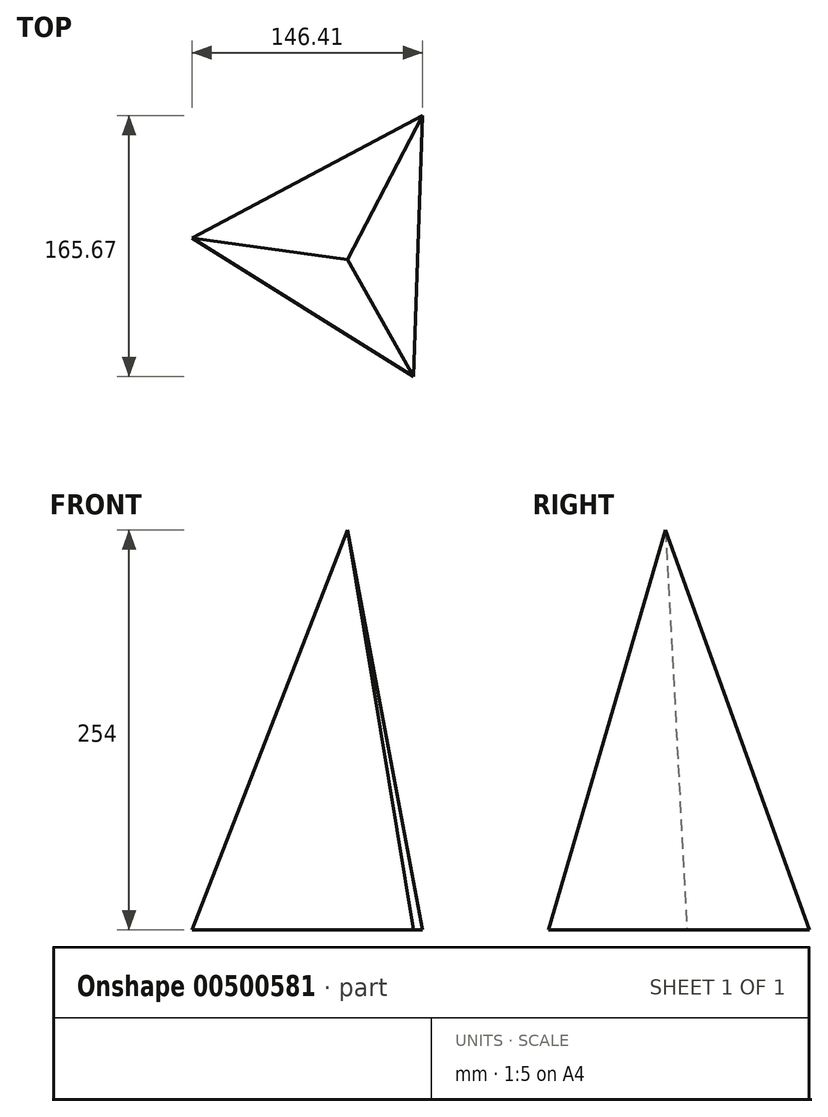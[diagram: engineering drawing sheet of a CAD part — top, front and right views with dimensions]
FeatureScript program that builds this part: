
annotation { "Feature Type Name" : "Feature", "Feature Type Description" : "" }
export const myFeature = defineFeature(function(context is Context, id is Id, definition is map)
    precondition{}
    {
        {
            var Q0;
            Q0=qCreatedBy(makeId("Top.planeOp"),FACE);
            var sketch = newSketch(context, id + "F0", { "sketchPlane" : qUnion([Q0])});
            skCircle(sketch, "E0.cCircle", {"center": v(0, 12.68) * mm, "radius": 95.7 * mm, "construction": true});
            skLineSegment(sketch, "E0.0", {"start": v(44.89, -71.85) * mm, "end": v(-95.65, 16.07) * mm});
            skLineSegment(sketch, "E0.1", {"start": v(-95.65, 16.07) * mm, "end": v(50.76, 93.82) * mm});
            skLineSegment(sketch, "E0.2", {"start": v(50.76, 93.82) * mm, "end": v(44.89, -71.85) * mm});
            skSolve(sketch);
        }
        {
            var Q0;
            Q0=qCreatedBy(makeId("Top.planeOp"),FACE);
            cPlane(context, id + "F1", {"entities" : qUnion([Q0]), "cplaneType" : CPlaneType.OFFSET, "offset" : 254 * mm, "width" : 152.4 * mm, "height" : 152.4 * mm});
        }
        {
            var Q0;
            Q0=qCreatedBy(id+"F1.planeOp",FACE);
            var sketch = newSketch(context, id + "F2", { "sketchPlane" : qUnion([Q0])});
            skPoint(sketch, "E1", {"position": v(3.2, 2.48) * mm});
            skSolve(sketch);
        }
        {
            var Q0;
            Q0=sQuery(id+"F2.wireOp",VERTEX,"E1");
            var Q1;
            Q1=makeQuery(id+"F0.imprint","IMPRINT",FACE,{"disambiguationData":[TD([[makeQuery(id+"F0.imprint","IMPRINT",EDGE,{"derivedFrom":sQuery(id+"F0.wireOp",EDGE,"E0.0")}),-1.0]])]});
            loft(context, id + "F3", {"sheetProfilesArray" : [{ "sheetProfileEntities" : qUnion([Q0]) }, { "sheetProfileEntities" : qUnion([Q1]) }]});
        }
    });
